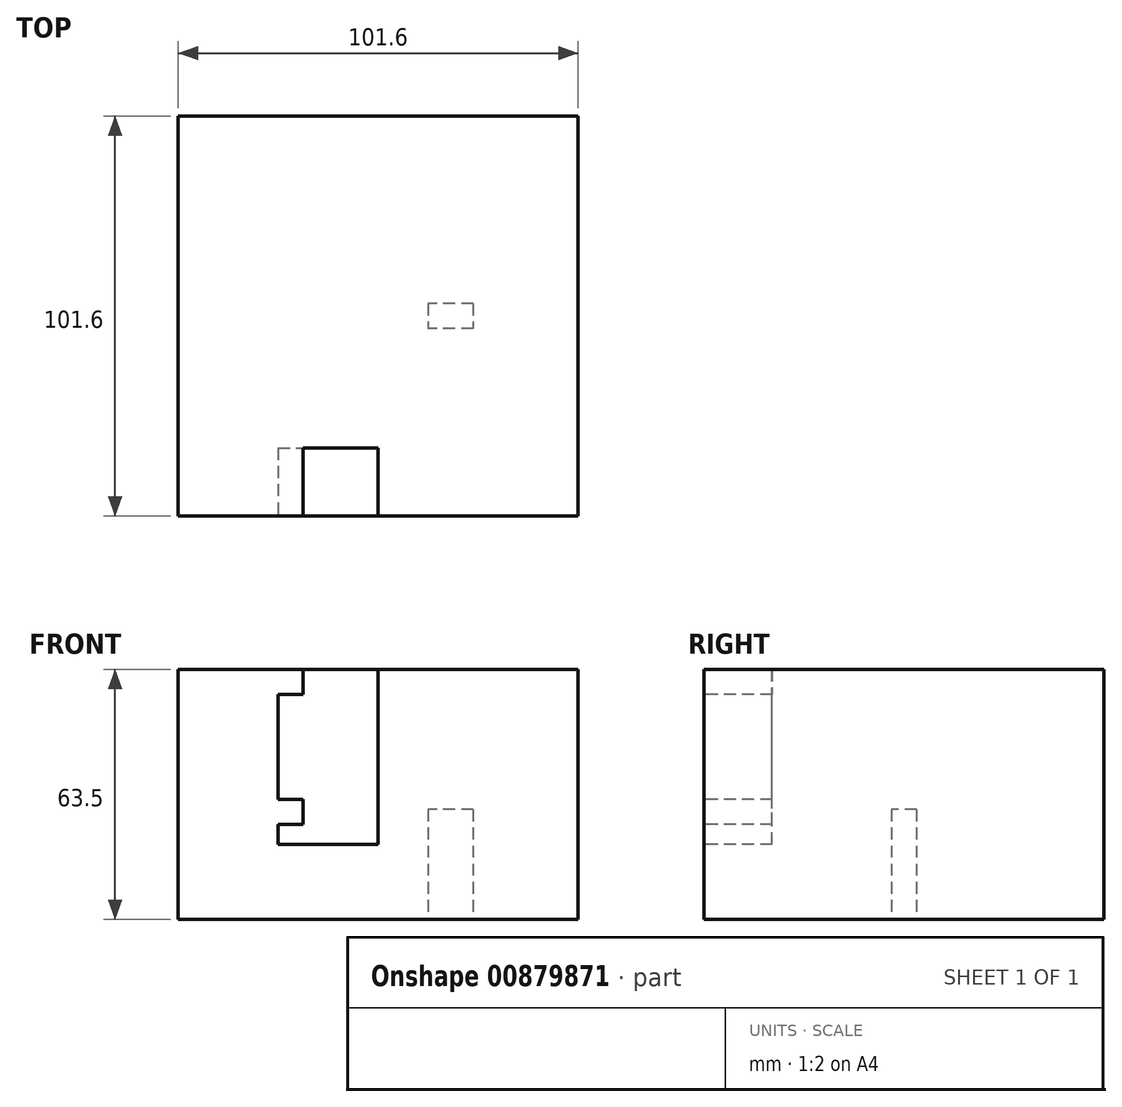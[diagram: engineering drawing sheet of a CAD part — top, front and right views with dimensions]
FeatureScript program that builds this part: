
annotation { "Feature Type Name" : "Feature", "Feature Type Description" : "" }
export const myFeature = defineFeature(function(context is Context, id is Id, definition is map)
    precondition{}
    {
        {
            var Q0;
            Q0=qCreatedBy(makeId("Top.planeOp"),FACE);
            var sketch = newSketch(context, id + "F0", { "sketchPlane" : qUnion([Q0])});
            skLineSegment(sketch, "E0.bottom", {"start": v(-50.8, 50.8) * mm, "end": v(50.8, 50.8) * mm});
            skLineSegment(sketch, "E0.top", {"start": v(-50.8, -50.8) * mm, "end": v(50.8, -50.8) * mm});
            skLineSegment(sketch, "E0.left", {"start": v(-50.8, 50.8) * mm, "end": v(-50.8, -50.8) * mm});
            skLineSegment(sketch, "E0.right", {"start": v(50.8, 50.8) * mm, "end": v(50.8, -50.8) * mm});
            skPoint(sketch, "E0.middle", {"position": v(0, 0) * mm});
            skSolve(sketch);
        }
        {
            var Q0;
            Q0=makeQuery(id+"F0.imprint","IMPRINT",FACE,{"disambiguationData":[TD([[makeQuery(id+"F0.imprint","IMPRINT",EDGE,{"derivedFrom":sQuery(id+"F0.wireOp",EDGE,"E0.bottom")}),-1.0]])]});
            extrude(context, id + "F1", {"entities" : qUnion([Q0]), "endBound" : BoundingType.SYMMETRIC, "depth" : 63.5 * mm, "offsetDistance" : 25.4 * mm});
        }
        {
            var Q0;
            Q0=makeQuery(id+"F1.opExtrude","CAP_FACE",FACE,{"disambiguationData":[OSD([sQuery(id+"F0.wireOp",EDGE,"E0.bottom"),sQuery(id+"F0.wireOp",EDGE,"E0.top"),sQuery(id+"F0.wireOp",EDGE,"E0.left"),sQuery(id+"F0.wireOp",EDGE,"E0.right")])],"isStart":true});
            var sketch = newSketch(context, id + "F2", { "sketchPlane" : qUnion([Q0])});
            skLineSegment(sketch, "E1", {"start": v(0, 0) * mm, "end": v(12.7, 0) * mm});
            skLineSegment(sketch, "E2", {"start": v(12.7, 0) * mm, "end": v(0, 0) * mm});
            skLineSegment(sketch, "E3", {"start": v(-27.94, 0) * mm, "end": v(0, 0) * mm});
            skLineSegment(sketch, "E4", {"start": v(12.7, 0) * mm, "end": v(12.7, -10.16) * mm});
            skLineSegment(sketch, "E5", {"start": v(12.7, -10.16) * mm, "end": v(12.7, 0) * mm});
            skLineSegment(sketch, "E6", {"start": v(-27.94, 0) * mm, "end": v(-27.94, 10.16) * mm});
            skLineSegment(sketch, "E7.bottom", {"start": v(12.7, -10.16) * mm, "end": v(-27.94, -10.16) * mm});
            skLineSegment(sketch, "E7.top", {"start": v(12.7, 10.16) * mm, "end": v(-27.94, 10.16) * mm});
            skLineSegment(sketch, "E7.left", {"start": v(12.7, -10.16) * mm, "end": v(12.7, 10.16) * mm});
            skLineSegment(sketch, "E7.right", {"start": v(-27.94, -10.16) * mm, "end": v(-27.94, 10.16) * mm});
            skLineSegment(sketch, "E8", {"start": v(12.7, 0) * mm, "end": v(24.13, 0) * mm});
            skLineSegment(sketch, "E9", {"start": v(24.13, 0) * mm, "end": v(24.13, 3.18) * mm});
            skLineSegment(sketch, "E10.bottom", {"start": v(24.13, 3.18) * mm, "end": v(12.7, 3.18) * mm});
            skLineSegment(sketch, "E10.top", {"start": v(24.13, -3.18) * mm, "end": v(12.7, -3.18) * mm});
            skLineSegment(sketch, "E10.left", {"start": v(24.13, 3.18) * mm, "end": v(24.13, -3.18) * mm});
            skLineSegment(sketch, "E10.right", {"start": v(12.7, 3.18) * mm, "end": v(12.7, -3.18) * mm});
            skPoint(sketch, "E10.middle", {"position": v(18.41, 0) * mm});
            skSolve(sketch);
        }
        {
            var Q0;
            {var subQ5=sQuery(id+"F2.wireOp",EDGE,"E2");Q0=makeQuery(id+"F2.imprint","IMPRINT",FACE,{"disambiguationData":[TD([[makeQuery(id+"F2.imprint","IMPRINT",EDGE,{"derivedFrom":subQ5}),1.0]])]});}
            var Q1;
            {var subQ5=sQuery(id+"F2.wireOp",EDGE,"E2");Q1=makeQuery(id+"F2.imprint","IMPRINT",FACE,{"disambiguationData":[TD([[makeQuery(id+"F2.imprint","IMPRINT",EDGE,{"derivedFrom":subQ5}),-1.0]])]});}
            var Q2;
            {var subQ0=sQuery(id+"F2.wireOp",EDGE,"E8");Q2=makeQuery(id+"F2.imprint","IMPRINT",FACE,{"disambiguationData":[TD([[makeQuery(id+"F2.imprint","IMPRINT",EDGE,{"derivedFrom":subQ0}),1.0]])]});}
            var Q3;
            {var subQ0=sQuery(id+"F2.wireOp",EDGE,"E8");Q3=makeQuery(id+"F2.imprint","IMPRINT",FACE,{"disambiguationData":[TD([[makeQuery(id+"F2.imprint","IMPRINT",EDGE,{"derivedFrom":subQ0}),-1.0]])]});}
            extrude(context, id + "F3", {"entities" : qUnion([Q0, Q1, Q2, Q3]), "operationType" : NewBodyOperationType.REMOVE, "oppositeDirection" : true, "depth" : 27.94 * mm, "offsetDistance" : 25.4 * mm});
        }
        {
            var Q0;
            Q0=makeQuery(id+"F1.opExtrude","SWEPT_FACE",FACE,{"disambiguationData":[OSD([sQuery(id+"F0.wireOp",EDGE,"E0.top")])]});
            var sketch = newSketch(context, id + "F4", { "sketchPlane" : qUnion([Q0])});
            skLineSegment(sketch, "E11", {"start": v(0, 0) * mm, "end": v(25.4, 0) * mm});
            skLineSegment(sketch, "E12", {"start": v(25.4, 0) * mm, "end": v(0, 0) * mm});
            skLineSegment(sketch, "E13", {"start": v(-38.1, 0) * mm, "end": v(0, 0) * mm});
            skLineSegment(sketch, "E14", {"start": v(0, 0) * mm, "end": v(0, 31.75) * mm});
            skLineSegment(sketch, "E15", {"start": v(0, 0) * mm, "end": v(0, -12.7) * mm});
            skLineSegment(sketch, "E16.bottom", {"start": v(-38.1, -12.7) * mm, "end": v(25.4, -12.7) * mm});
            skLineSegment(sketch, "E16.top", {"start": v(-38.1, 31.75) * mm, "end": v(25.4, 31.75) * mm});
            skLineSegment(sketch, "E16.left", {"start": v(-38.1, -12.7) * mm, "end": v(-38.1, 31.75) * mm});
            skLineSegment(sketch, "E16.right", {"start": v(25.4, -12.7) * mm, "end": v(25.4, 31.75) * mm});
            skLineSegment(sketch, "E17", {"start": v(-38.1, -12.7) * mm, "end": v(-25.4, -12.7) * mm});
            skLineSegment(sketch, "E18", {"start": v(-25.4, -12.7) * mm, "end": v(-25.4, 31.75) * mm});
            skLineSegment(sketch, "E19.bottom", {"start": v(-25.4, 31.75) * mm, "end": v(-19.05, 31.75) * mm});
            skLineSegment(sketch, "E19.top", {"start": v(-25.4, 25.4) * mm, "end": v(-19.05, 25.4) * mm});
            skLineSegment(sketch, "E19.left", {"start": v(-25.4, 31.75) * mm, "end": v(-25.4, 25.4) * mm});
            skLineSegment(sketch, "E19.right", {"start": v(-19.05, 31.75) * mm, "end": v(-19.05, 25.4) * mm});
            skLineSegment(sketch, "E20.bottom", {"start": v(25.4, 31.75) * mm, "end": v(19.05, 31.75) * mm});
            skLineSegment(sketch, "E20.top", {"start": v(25.4, 25.4) * mm, "end": v(19.05, 25.4) * mm});
            skLineSegment(sketch, "E20.left", {"start": v(25.4, 31.75) * mm, "end": v(25.4, 25.4) * mm});
            skLineSegment(sketch, "E20.right", {"start": v(19.05, 31.75) * mm, "end": v(19.05, 25.4) * mm});
            skLineSegment(sketch, "E21", {"start": v(-25.4, -12.7) * mm, "end": v(-25.4, -7.62) * mm});
            skPoint(sketch, "E22.oppositeSnap0", {"position": v(-19.05, 0) * mm});
            skLineSegment(sketch, "E22.bottom", {"start": v(-25.4, -7.62) * mm, "end": v(-19.05, -7.62) * mm});
            skLineSegment(sketch, "E22.top", {"start": v(-25.4, -1.27) * mm, "end": v(-19.05, -1.27) * mm});
            skLineSegment(sketch, "E22.left", {"start": v(-25.4, -7.62) * mm, "end": v(-25.4, -1.27) * mm});
            skLineSegment(sketch, "E22.right", {"start": v(-19.05, -7.62) * mm, "end": v(-19.05, -1.27) * mm});
            skSolve(sketch);
        }
        {
            var Q0;
            {var subQ3=sQuery(id+"F4.wireOp",EDGE,"E19.left");Q0=makeQuery(id+"F4.imprint","IMPRINT",FACE,{"disambiguationData":[TD([[makeQuery(id+"F4.imprint","IMPRINT",EDGE,{"derivedFrom":subQ3}),-1.0]])]});}
            var Q1;
            {var subQ5=sQuery(id+"F4.wireOp",EDGE,"E14");Q1=makeQuery(id+"F4.imprint","IMPRINT",FACE,{"disambiguationData":[TD([[makeQuery(id+"F4.imprint","IMPRINT",EDGE,{"derivedFrom":subQ5}),1.0]])]});}
            var Q2;
            {var subQ4=sQuery(id+"F4.wireOp",EDGE,"E12");Q2=makeQuery(id+"F4.imprint","IMPRINT",FACE,{"disambiguationData":[TD([[makeQuery(id+"F4.imprint","IMPRINT",EDGE,{"derivedFrom":subQ4}),-1.0]])]});}
            var Q3;
            {var subQ0=sQuery(id+"F4.wireOp",EDGE,"E12");Q3=makeQuery(id+"F4.imprint","IMPRINT",FACE,{"disambiguationData":[TD([[makeQuery(id+"F4.imprint","IMPRINT",EDGE,{"derivedFrom":subQ0}),1.0]])]});}
            var Q4;
            {var subQ4=sQuery(id+"F4.wireOp",EDGE,"E15");Q4=makeQuery(id+"F4.imprint","IMPRINT",FACE,{"disambiguationData":[TD([[makeQuery(id+"F4.imprint","IMPRINT",EDGE,{"derivedFrom":subQ4}),-1.0]])]});}
            extrude(context, id + "F5", {"entities" : qUnion([Q0, Q1, Q2, Q3, Q4]), "operationType" : NewBodyOperationType.REMOVE, "oppositeDirection" : true, "depth" : 17.27 * mm, "offsetDistance" : 25.4 * mm});
        }
    });
